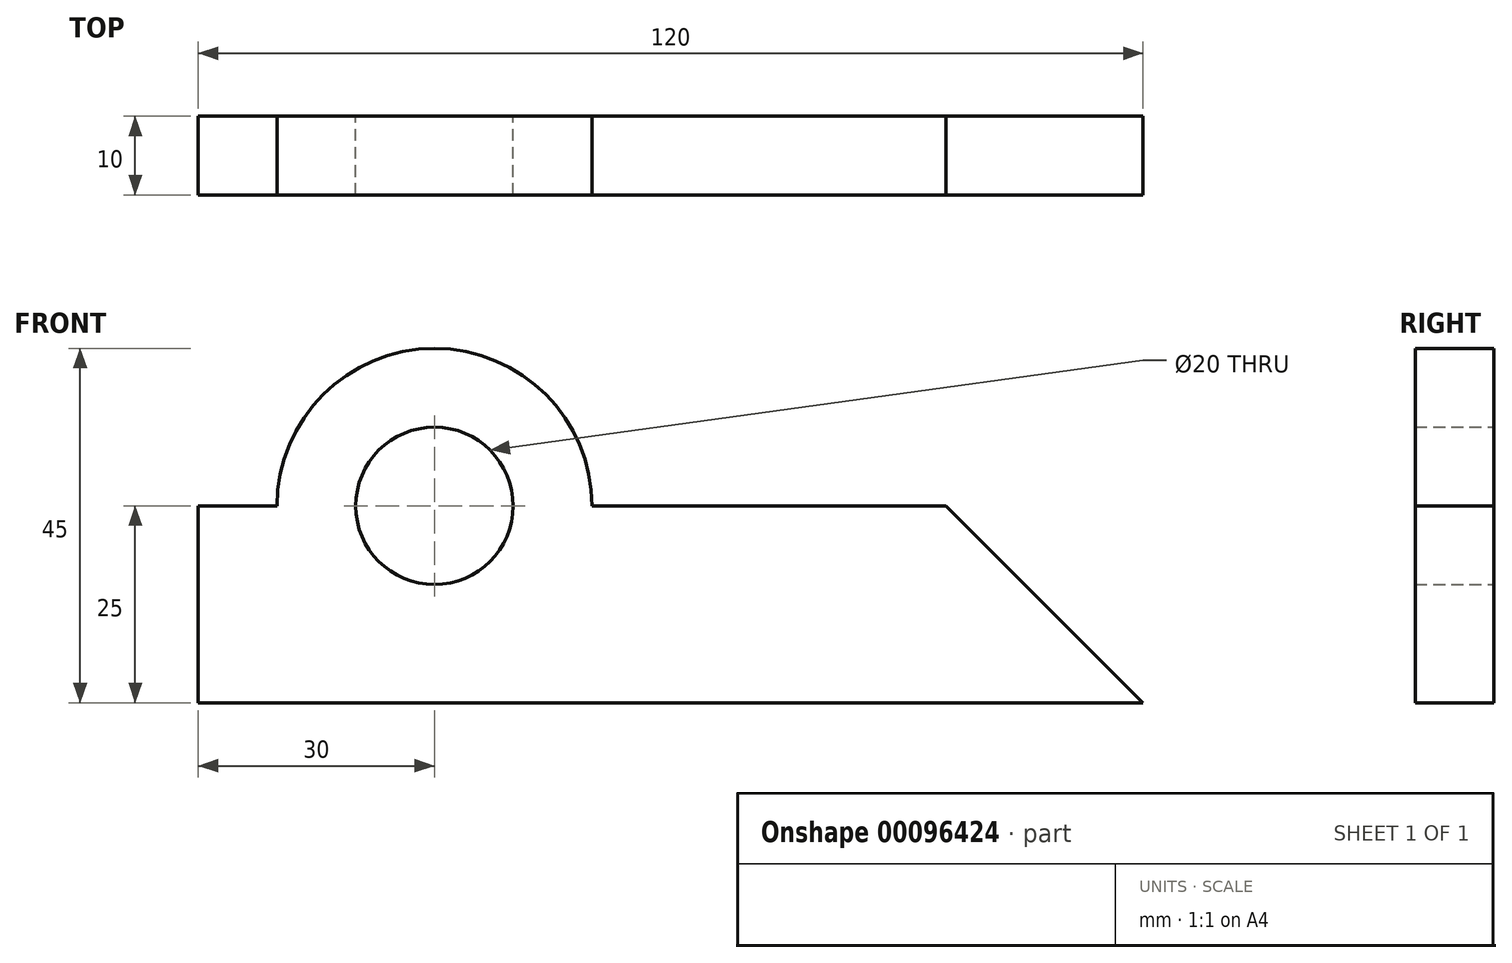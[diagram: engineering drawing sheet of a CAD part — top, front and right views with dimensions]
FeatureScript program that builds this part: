
annotation { "Feature Type Name" : "Feature", "Feature Type Description" : "" }
export const myFeature = defineFeature(function(context is Context, id is Id, definition is map)
    precondition{}
    {
        {
            var Q0;
            Q0=qCreatedBy(makeId("Front.planeOp"),FACE);
            var sketch = newSketch(context, id + "F0", { "sketchPlane" : qUnion([Q0])});
            skLineSegment(sketch, "E0", {"start": v(0, 0) * mm, "end": v(0, 25) * mm});
            skLineSegment(sketch, "E1", {"start": v(0, 0) * mm, "end": v(120, 0) * mm});
            skLineSegment(sketch, "E2", {"start": v(120, 0) * mm, "end": v(95, 25) * mm});
            skLineSegment(sketch, "E3", {"start": v(0, 25) * mm, "end": v(95, 25) * mm, "construction": true});
            skCircle(sketch, "E4", {"center": v(30, 25) * mm, "radius": 10 * mm});
            skArc(sketch, "E5", {"start": v(50, 25) * mm, "mid": v(30, 45) * mm, "end": v(10, 25) * mm});
            skLineSegment(sketch, "E6", {"start": v(0, 25) * mm, "end": v(10, 25) * mm});
            skLineSegment(sketch, "E7", {"start": v(50, 25) * mm, "end": v(95, 25) * mm});
            skSolve(sketch);
        }
        {
            var Q0;
            Q0 = qSketchRegion(id + "F0", true);
            extrude(context, id + "F1", {"entities" : qUnion([Q0]), "endBound" : BoundingType.SYMMETRIC, "depth" : 10 * mm});
        }
    });
